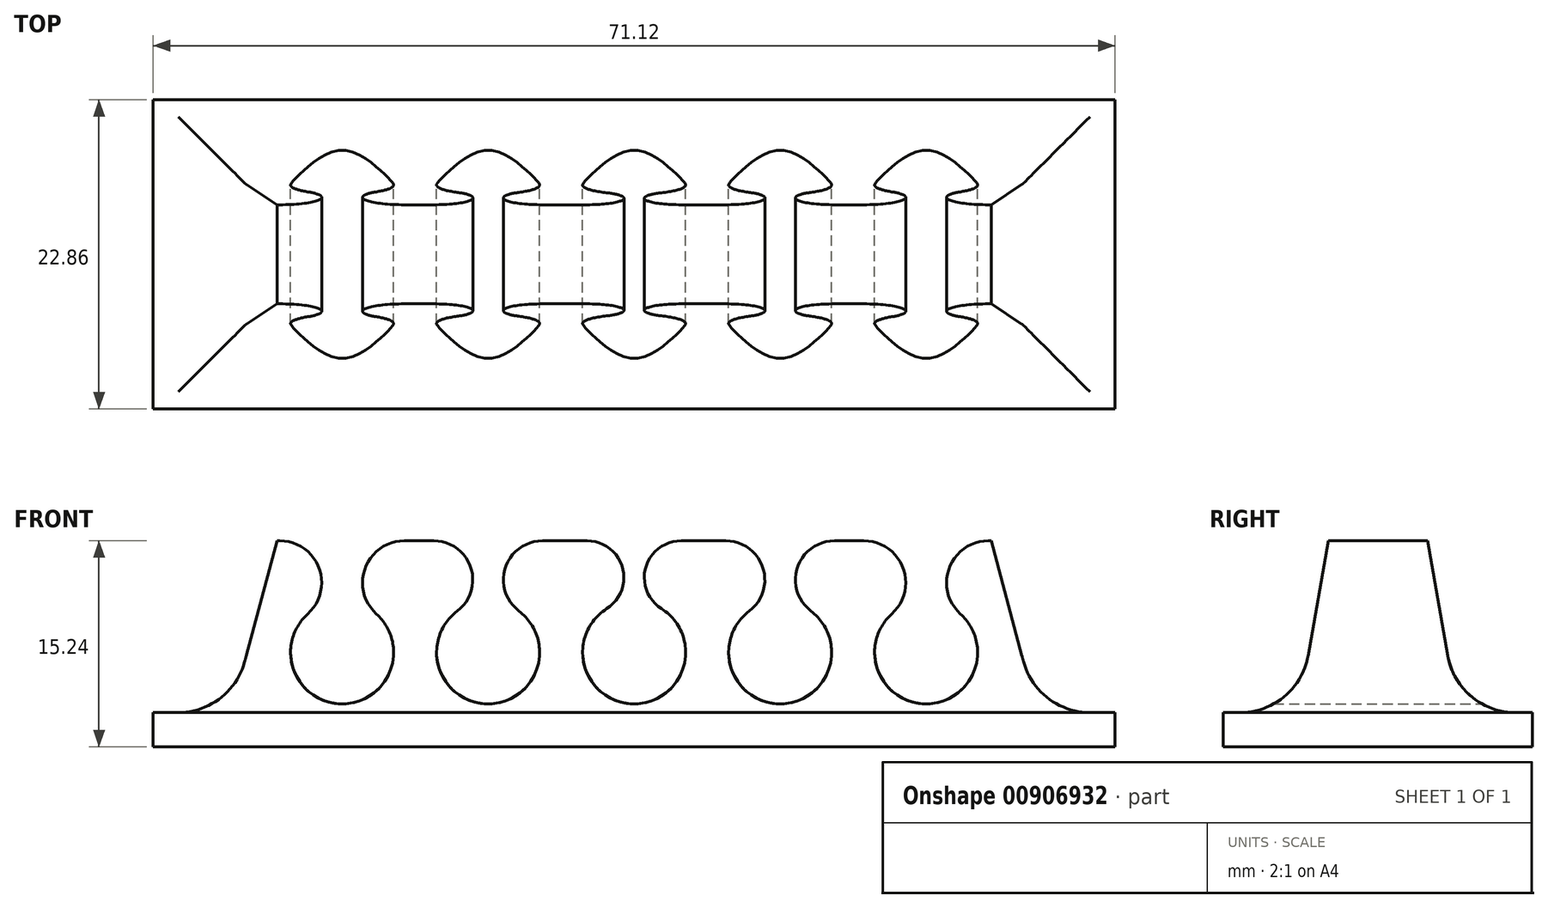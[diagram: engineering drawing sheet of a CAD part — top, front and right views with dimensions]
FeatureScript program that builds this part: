
annotation { "Feature Type Name" : "Feature", "Feature Type Description" : "" }
export const myFeature = defineFeature(function(context is Context, id is Id, definition is map)
    precondition{}
    {
        {
            var Q0;
            Q0=qCreatedBy(makeId("Front.planeOp"),FACE);
            var sketch = newSketch(context, id + "F0", { "sketchPlane" : qUnion([Q0])});
            skLineSegment(sketch, "E0", {"start": v(-30.48, 0) * mm, "end": v(30.48, 0) * mm});
            skPoint(sketch, "E1", {"position": v(0, 0) * mm});
            skLineSegment(sketch, "E2", {"start": v(-30.48, 0) * mm, "end": v(-26.4, 15.24) * mm});
            skArc(sketch, "E3", {"start": v(-2.03, 10.21) * mm, "mid": v(0, 3.17) * mm, "end": v(2.03, 10.21) * mm});
            skArc(sketch, "E4", {"start": v(-2.03, 10.21) * mm, "mid": v(-0.86, 13.27) * mm, "end": v(-3.47, 15.24) * mm});
            skLineSegment(sketch, "E5", {"start": v(-26.4, 15.24) * mm, "end": v(-26.19, 15.24) * mm});
            skArc(sketch, "E6.MirrorCS", {"start": v(2.03, 10.21) * mm, "mid": v(0.86, 13.27) * mm, "end": v(3.47, 15.24) * mm});
            skLineSegment(sketch, "E7.MirrorCS", {"start": v(30.48, 0) * mm, "end": v(26.4, 15.24) * mm});
            skLineSegment(sketch, "E8", {"start": v(26.4, 15.24) * mm, "end": v(26.19, 15.24) * mm});
            skLineSegment(sketch, "E9.direction1", {"start": v(0, 6.99) * mm, "end": v(10.8, 6.99) * mm, "construction": true});
            skArc(sketch, "E10.MirrorCS", {"start": v(-8.51, 10.03) * mm, "mid": v(-10.8, 3.17) * mm, "end": v(-13.08, 10.03) * mm});
            skArc(sketch, "E11.MirrorCS", {"start": v(-13.08, 10.03) * mm, "mid": v(-12.07, 13.26) * mm, "end": v(-14.81, 15.24) * mm});
            skArc(sketch, "E12.MirrorCS", {"start": v(-8.51, 10.03) * mm, "mid": v(-9.52, 13.26) * mm, "end": v(-6.78, 15.24) * mm});
            skLineSegment(sketch, "E13.trimOffspring", {"start": v(-17, 15.24) * mm, "end": v(-14.81, 15.24) * mm});
            skLineSegment(sketch, "E14.trimOffspring", {"start": v(-6.78, 15.24) * mm, "end": v(-3.47, 15.24) * mm});
            skLineSegment(sketch, "E15.trimOffspring", {"start": v(7.32, 15.24) * mm, "end": v(3.47, 15.24) * mm});
            skArc(sketch, "E16", {"start": v(-24.13, 9.83) * mm, "mid": v(-23.3, 13.24) * mm, "end": v(-26.19, 15.24) * mm});
            skArc(sketch, "E17", {"start": v(-17, 15.24) * mm, "mid": v(-19.89, 13.24) * mm, "end": v(-19.05, 9.83) * mm});
            skArc(sketch, "E18", {"start": v(-24.13, 9.83) * mm, "mid": v(-21.59, 3.17) * mm, "end": v(-19.05, 9.83) * mm});
            skLineSegment(sketch, "E19.MirrorCS", {"start": v(6.78, 15.24) * mm, "end": v(3.47, 15.24) * mm});
            skLineSegment(sketch, "E20.MirrorCS", {"start": v(17, 15.24) * mm, "end": v(14.81, 15.24) * mm});
            skArc(sketch, "E21.MirrorCS", {"start": v(13.08, 10.03) * mm, "mid": v(12.07, 13.26) * mm, "end": v(14.81, 15.24) * mm});
            skArc(sketch, "E22.MirrorCS", {"start": v(24.13, 9.83) * mm, "mid": v(21.59, 3.17) * mm, "end": v(19.05, 9.83) * mm});
            skArc(sketch, "E23.MirrorCS", {"start": v(8.51, 10.03) * mm, "mid": v(10.8, 3.17) * mm, "end": v(13.08, 10.03) * mm});
            skArc(sketch, "E24.MirrorCS", {"start": v(8.51, 10.03) * mm, "mid": v(9.52, 13.26) * mm, "end": v(6.78, 15.24) * mm});
            skArc(sketch, "E25.MirrorCS", {"start": v(17, 15.24) * mm, "mid": v(19.89, 13.24) * mm, "end": v(19.05, 9.83) * mm});
            skArc(sketch, "E26.MirrorCS", {"start": v(24.13, 9.83) * mm, "mid": v(23.3, 13.24) * mm, "end": v(26.19, 15.24) * mm});
            skSolve(sketch);
        }
        {
            var Q0;
            Q0=makeQuery(id+"F0.imprint","IMPRINT",FACE,{"disambiguationData":[TD([[makeQuery(id+"F0.imprint","IMPRINT",EDGE,{"derivedFrom":sQuery(id+"F0.wireOp",EDGE,"E0")}),1.0]])]});
            extrude(context, id + "F1", {"entities" : qUnion([Q0]), "depth" : 12.7 * mm, "offsetDistance" : 25.4 * mm});
        }
        {
            var Q0;
            Q0=qCreatedBy(makeId("Right.planeOp"),FACE);
            var sketch = newSketch(context, id + "F2", { "sketchPlane" : qUnion([Q0])});
            skLineSegment(sketch, "E27", {"start": v(0, 0) * mm, "end": v(-12.7, 0) * mm});
            skLineSegment(sketch, "E28", {"start": v(-12.7, 0) * mm, "end": v(-10.01, 15.24) * mm});
            skLineSegment(sketch, "E29", {"start": v(-6.35, 0) * mm, "end": v(-6.35, 16.1) * mm, "construction": true});
            skLineSegment(sketch, "E30.MirrorCS", {"start": v(0, 0) * mm, "end": v(-2.69, 15.24) * mm});
            skLineSegment(sketch, "E31", {"start": v(-10.01, 15.24) * mm, "end": v(-2.69, 15.24) * mm});
            skLineSegment(sketch, "E32", {"start": v(-2.69, 15.24) * mm, "end": v(0, 15.24) * mm});
            skLineSegment(sketch, "E33", {"start": v(0, 15.24) * mm, "end": v(0, 0) * mm});
            skLineSegment(sketch, "E34", {"start": v(-10.01, 15.24) * mm, "end": v(-12.7, 15.24) * mm});
            skLineSegment(sketch, "E35", {"start": v(-12.7, 15.24) * mm, "end": v(-12.7, 0) * mm});
            skSolve(sketch);
        }
        {
            var Q0;
            Q0=makeQuery(id+"F2.imprint","IMPRINT",FACE,{"disambiguationData":[TD([[makeQuery(id+"F2.imprint","IMPRINT",EDGE,{"derivedFrom":sQuery(id+"F2.wireOp",EDGE,"E28")}),1.0]])]});
            var Q1;
            Q1=makeQuery(id+"F2.imprint","IMPRINT",FACE,{"disambiguationData":[TD([[makeQuery(id+"F2.imprint","IMPRINT",EDGE,{"derivedFrom":sQuery(id+"F2.wireOp",EDGE,"E30.MirrorCS")}),-1.0]])]});
            extrude(context, id + "F3", {"entities" : qUnion([Q0, Q1]), "operationType" : NewBodyOperationType.REMOVE, "endBound" : BoundingType.THROUGH_ALL, "oppositeDirection" : true, "depth" : 25.4 * mm, "offsetDistance" : 25.4 * mm, "hasSecondDirection" : true, "secondDirectionBound" : SecondDirectionBoundingType.THROUGH_ALL, "secondDirectionOppositeDirection" : false, "secondDirectionDepth" : 25.4 * mm});
        }
        {
            var Q0;
            Q0=makeQuery(id+"F1.opExtrude","SWEPT_FACE",FACE,{"disambiguationData":[OSD([sQuery(id+"F0.wireOp",EDGE,"E0")])]});
            var sketch = newSketch(context, id + "F4", { "sketchPlane" : qUnion([Q0])});
            skLineSegment(sketch, "E36", {"start": v(0, 12.7) * mm, "end": v(0, 0) * mm, "construction": true});
            skLineSegment(sketch, "E37.bottom", {"start": v(35.56, 17.78) * mm, "end": v(-35.56, 17.78) * mm});
            skLineSegment(sketch, "E37.top", {"start": v(35.56, -5.08) * mm, "end": v(-35.56, -5.08) * mm});
            skLineSegment(sketch, "E37.left", {"start": v(35.56, 17.78) * mm, "end": v(35.56, -5.08) * mm});
            skLineSegment(sketch, "E37.right", {"start": v(-35.56, 17.78) * mm, "end": v(-35.56, -5.08) * mm});
            skPoint(sketch, "E37.middle", {"position": v(0, 6.35) * mm});
            skSolve(sketch);
        }
        {
            var Q0;
            Q0=makeQuery(id+"F4.imprint","IMPRINT",FACE,{"disambiguationData":[TD([[makeQuery(id+"F4.imprint","IMPRINT",EDGE,{"derivedFrom":sQuery(id+"F4.wireOp",EDGE,"E37.bottom")}),1.0]])]});
            var Q1;
            {var subQ0=sQuery(id+"F0.wireOp",EDGE,"E0");Q1=makeQuery(id+"F4.imprint","IMPRINT",FACE,{"disambiguationData":[TD([[makeQuery(id+"F4.imprint","IMPRINT",EDGE,{"derivedFrom":makeQuery(id+"F1.opExtrude","SWEPT_EDGE",EDGE,{"disambiguationData":[OSD([subQ0,sQuery(id+"F0.wireOp",EDGE,"E2")])]})}),1.0]])]});}
            extrude(context, id + "F5", {"entities" : qUnion([Q0, Q1]), "operationType" : NewBodyOperationType.ADD, "oppositeDirection" : true, "depth" : 2.54 * mm, "offsetDistance" : 25.4 * mm});
        }
        {
            var Q0;
            Q0=makeQuery(id+"F5.boolean.opBoolean","INTERSECT",EDGE,{"derivedFrom":[makeQuery(id+"F3.boolean.opBoolean","COPY",FACE,{"derivedFrom":makeQuery(id+"F3.opExtrude","SWEPT_FACE",FACE,{"disambiguationData":[OSD([sQuery(id+"F2.wireOp",EDGE,"E28")])]})}),makeQuery(id+"F5.opExtrude","CAP_FACE",FACE,{"disambiguationData":[OSD([sQuery(id+"F4.wireOp",EDGE,"E37.bottom"),sQuery(id+"F4.wireOp",EDGE,"E37.top"),sQuery(id+"F4.wireOp",EDGE,"E37.left"),sQuery(id+"F4.wireOp",EDGE,"E37.right")])],"isStart":false})]});
            var Q1;
            Q1=makeQuery(id+"F5.boolean.opBoolean","INTERSECT",EDGE,{"derivedFrom":[makeQuery(id+"F1.opExtrude","SWEPT_FACE",FACE,{"disambiguationData":[OSD([sQuery(id+"F0.wireOp",EDGE,"E2")])]}),makeQuery(id+"F5.opExtrude","CAP_FACE",FACE,{"disambiguationData":[OSD([sQuery(id+"F4.wireOp",EDGE,"E37.bottom"),sQuery(id+"F4.wireOp",EDGE,"E37.top"),sQuery(id+"F4.wireOp",EDGE,"E37.left"),sQuery(id+"F4.wireOp",EDGE,"E37.right")])],"isStart":false})]});
            var Q2;
            Q2=makeQuery(id+"F5.boolean.opBoolean","INTERSECT",EDGE,{"derivedFrom":[makeQuery(id+"F3.boolean.opBoolean","COPY",FACE,{"derivedFrom":makeQuery(id+"F3.opExtrude","SWEPT_FACE",FACE,{"disambiguationData":[OSD([sQuery(id+"F2.wireOp",EDGE,"E30.MirrorCS")])]})}),makeQuery(id+"F5.opExtrude","CAP_FACE",FACE,{"disambiguationData":[OSD([sQuery(id+"F4.wireOp",EDGE,"E37.bottom"),sQuery(id+"F4.wireOp",EDGE,"E37.top"),sQuery(id+"F4.wireOp",EDGE,"E37.left"),sQuery(id+"F4.wireOp",EDGE,"E37.right")])],"isStart":false})]});
            var Q3;
            Q3=makeQuery(id+"F5.boolean.opBoolean","INTERSECT",EDGE,{"derivedFrom":[makeQuery(id+"F1.opExtrude","SWEPT_FACE",FACE,{"disambiguationData":[OSD([sQuery(id+"F0.wireOp",EDGE,"E7.MirrorCS")])]}),makeQuery(id+"F5.opExtrude","CAP_FACE",FACE,{"disambiguationData":[OSD([sQuery(id+"F4.wireOp",EDGE,"E37.bottom"),sQuery(id+"F4.wireOp",EDGE,"E37.top"),sQuery(id+"F4.wireOp",EDGE,"E37.left"),sQuery(id+"F4.wireOp",EDGE,"E37.right")])],"isStart":false})]});
            fillet(context, id + "F6", {"entities" : qUnion([Q0, Q1, Q2, Q3]), "radius" : 5.08 * mm, "tangentPropagation" : true, "allowEdgeOverflow" : false});
        }
        {
            var Q0;
            Q0=qCreatedBy(makeId("Right.planeOp"),FACE);
            cPlane(context, id + "F7", {"entities" : qUnion([Q0]), "cplaneType" : CPlaneType.OFFSET, "offset" : 5.33 * mm, "width" : 152.4 * mm, "height" : 152.4 * mm});
        }
        {
            var Q0;
            Q0=qCreatedBy(makeId("Right.planeOp"),FACE);
            cPlane(context, id + "F8", {"entities" : qUnion([Q0]), "cplaneType" : CPlaneType.OFFSET, "offset" : 5.33 * mm, "oppositeDirection" : true, "width" : 152.4 * mm, "height" : 152.4 * mm});
        }
    });
